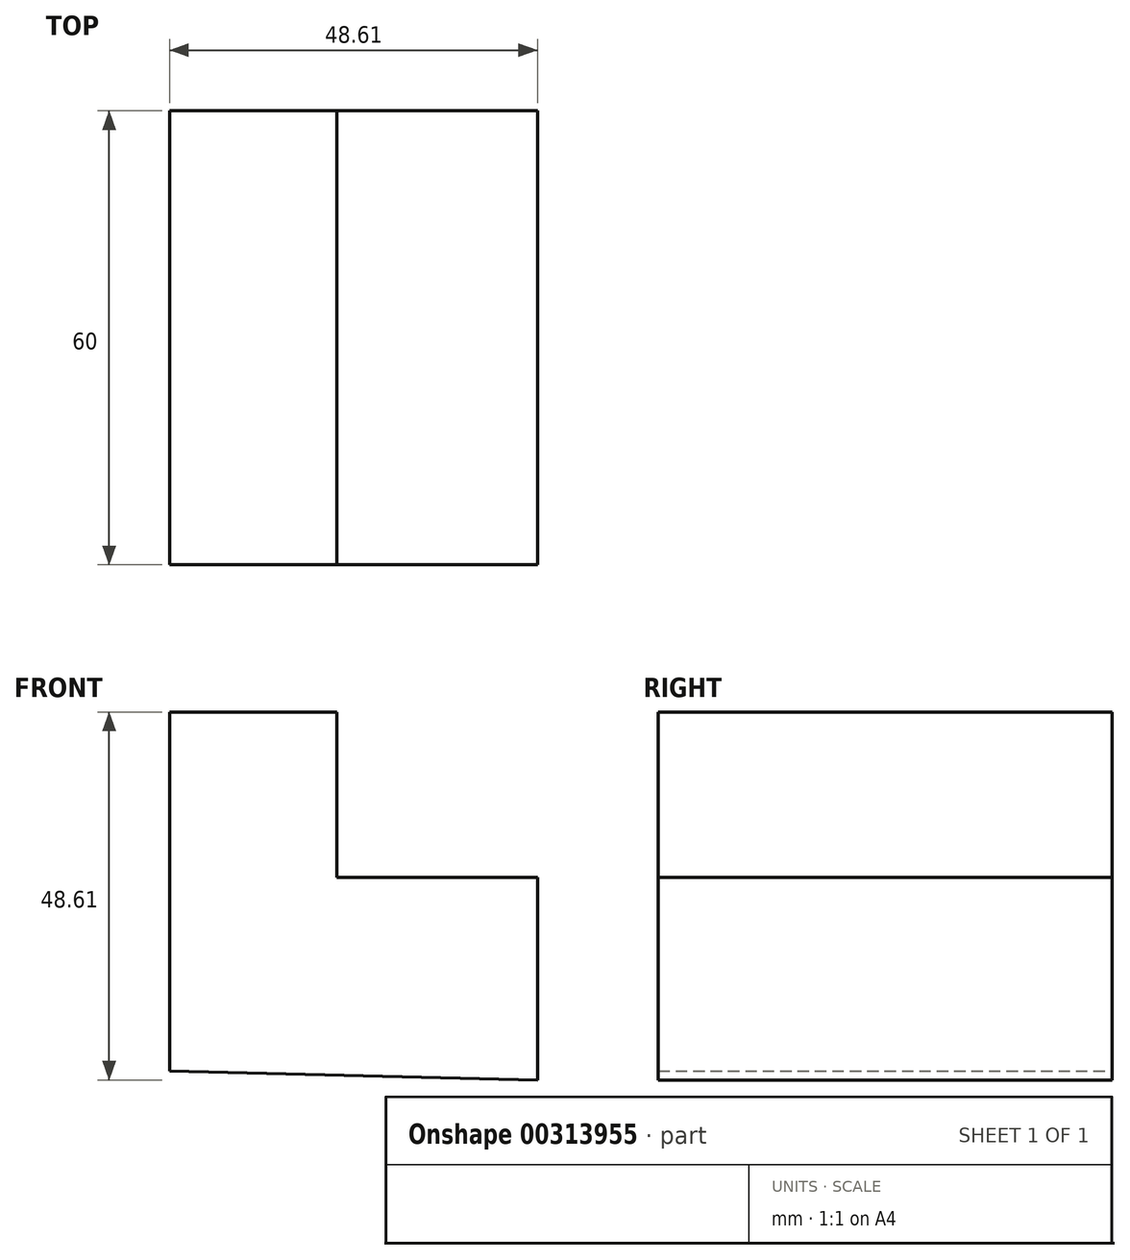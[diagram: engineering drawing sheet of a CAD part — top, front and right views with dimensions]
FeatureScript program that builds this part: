
annotation { "Feature Type Name" : "Feature", "Feature Type Description" : "" }
export const myFeature = defineFeature(function(context is Context, id is Id, definition is map)
    precondition{}
    {
        {
            var Q0;
            Q0=qCreatedBy(makeId("Front.planeOp"),FACE);
            var sketch = newSketch(context, id + "F0", { "sketchPlane" : qUnion([Q0])});
            skLineSegment(sketch, "E0", {"start": v(-46.98, 36.75) * mm, "end": v(-24.89, 36.75) * mm});
            skLineSegment(sketch, "E1", {"start": v(-24.89, 36.75) * mm, "end": v(-24.89, 14.89) * mm});
            skLineSegment(sketch, "E2", {"start": v(-24.89, 14.89) * mm, "end": v(1.63, 14.89) * mm});
            skLineSegment(sketch, "E3", {"start": v(1.63, 14.89) * mm, "end": v(1.63, -11.86) * mm});
            skLineSegment(sketch, "E4", {"start": v(-46.98, 36.75) * mm, "end": v(-46.98, -10.7) * mm});
            skLineSegment(sketch, "E5", {"start": v(-46.98, -10.7) * mm, "end": v(1.63, -11.86) * mm});
            skSolve(sketch);
        }
        {
            var Q0;
            Q0=makeQuery(id+"F0.imprint","IMPRINT",FACE,{"disambiguationData":[TD([[makeQuery(id+"F0.imprint","IMPRINT",EDGE,{"derivedFrom":sQuery(id+"F0.wireOp",EDGE,"E0")}),-1.0]])]});
            extrude(context, id + "F1", {"entities" : qUnion([Q0]), "depth" : 60 * mm});
        }
    });
